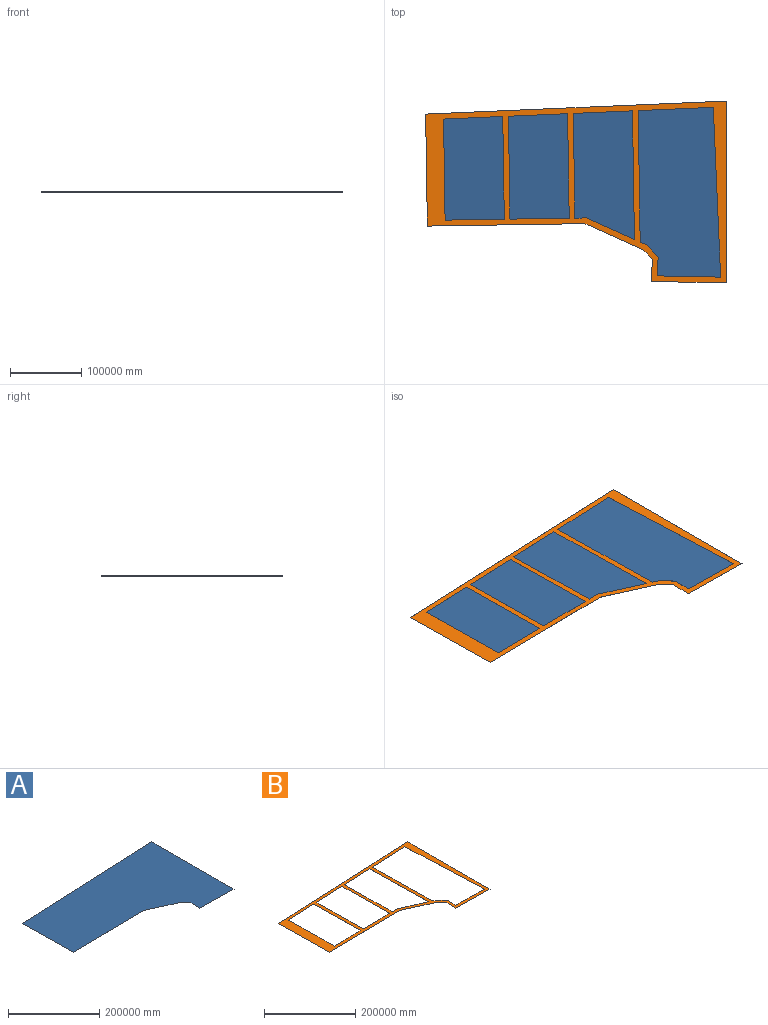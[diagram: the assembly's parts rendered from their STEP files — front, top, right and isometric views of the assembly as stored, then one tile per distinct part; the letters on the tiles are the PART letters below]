
ASSEMBLY  parts=2 mates=1
PART A: 10 faces, bbox 421603.4x255000x25 mm
  f0: plane 421603.41x18291.14mm, normal (-0.04,1,0), area 10550000mm2, adj f1,f7,f8,f9
  f1: plane 156981.63x2401.73mm, normal (-1,-0.02,0), area 3925000mm2, adj f0,f2,f8,f9
  f2: plane 220974.14x3380.78mm, normal (0.02,-1,0), area 5525000mm2, adj f1,f3,f8,f9
  f3: plane 81227.35x36374.69mm, normal (-0.41,-0.91,0), area 2225000mm2, adj f2,f4,f8,f9
  f4: plane 13695.87x13169.02mm, normal (-0.72,-0.69,0), area 475000mm2, adj f3,f5,f8,f9
  f5: plane 30978.71x1148.65mm, normal (-1,0.04,0), area 775000mm2, adj f4,f6,f8,f9
  f6: plane 104979.82x2058.74mm, normal (-0.02,-1,0), area 2625000mm2, adj f5,f7,f8,f9
  f7: plane 255000x25mm, normal (1,0,0), area 6375000mm2, adj f0,f6,f8,f9
  f8: plane 421603.41x255000mm, normal (0,0,1), area 79395387368.9mm2, adj f0,f1,f2,f3,f4,f5,f6,f7
  f9: plane 421603.41x255000mm, normal (0,0,-1), area 79395387368.9mm2, adj f0,f1,f2,f3,f4,f5,f6,f7
PART B: 30 faces, bbox 421603.4x255000x25 mm
  f0: plane 421603.41x18291.14mm, normal (-0.04,1,0), area 10550000mm2, adj f1,f27,f28,f29
  f1: plane 156981.63x2401.73mm, normal (-1,-0.02,0), area 3925000mm2, adj f0,f2,f28,f29
  f2: plane 220974.14x3380.78mm, normal (0.02,-1,0), area 5525000mm2, adj f1,f3,f28,f29
  f3: plane 81227.35x36374.69mm, normal (-0.41,-0.91,0), area 2225000mm2, adj f2,f4,f28,f29
  f4: plane 13695.87x13169.02mm, normal (-0.72,-0.69,0), area 475000mm2, adj f3,f5,f28,f29
  f5: plane 30978.71x1148.65mm, normal (-1,0.04,0), area 775000mm2, adj f4,f6,f28,f29
  f6: plane 104979.82x2058.74mm, normal (-0.02,-1,0), area 2625000mm2, adj f5,f27,f28,f29
  f7: plane 141681.93x2167.66mm, normal (1,0.02,0), area 3542462.9mm2, adj f8,f23,f28,f29
  f8: plane 82954.65x3598.96mm, normal (0.04,-1,0), area 2075817.1mm2, adj f7,f9,f28,f29
  f9: plane 144011.19x2203.29mm, normal (-1,-0.02,0), area 3600701.1mm2, adj f8,f23,f28,f29
  f10: plane 144235.7x2206.73mm, normal (1,0.02,0), area 3606314.4mm2, adj f11,f24,f28,f29
  f11: plane 82954.65x3598.96mm, normal (0.04,-1,0), area 2075817.1mm2, adj f10,f12,f28,f29
  f12: plane 146564.96x2242.36mm, normal (-1,-0.02,0), area 3664552.7mm2, adj f11,f24,f28,f29
  f13: plane 15771.71x241.3mm, normal (-0.02,1,0), area 394338.9mm2, adj f14,f25,f28,f29
  f14: plane 146789.46x2245.8mm, normal (1,0.02,0), area 3670166mm2, adj f13,f15,f28,f29
  f15: plane 82954.65x3598.96mm, normal (0.04,-1,0), area 2075817.1mm2, adj f14,f16,f28,f29
  f16: plane 180463.26x2760.99mm, normal (-1,-0.02,0), area 4512109.4mm2, adj f15,f25,f28,f29
  f17: plane 8510.99x3811.33mm, normal (0.41,0.91,0), area 233135.1mm2, adj f18,f26,f28,f29
  f18: plane 184417.79x2821.49mm, normal (1,0.02,0), area 4610984.2mm2, adj f17,f19,f28,f29
  f19: plane 105316.55x4569.13mm, normal (0.04,-1,0), area 2635390.5mm2, adj f18,f20,f28,f29
  f20: plane 238038.93x10327.25mm, normal (-1,-0.04,0), area 5956571.1mm2, adj f19,f21,f28,f29
  f21: plane 88683.66x1739.16mm, normal (0.02,1,0), area 2217517.9mm2, adj f20,f22,f28,f29
  f22: plane 26236.91x972.83mm, normal (1,-0.04,0), area 656373.5mm2, adj f21,f26,f28,f29
  f23: plane 82990.29x1269.71mm, normal (-0.02,1,0), area 2075000mm2, adj f7,f9,f28,f29
  f24: plane 82990.29x1269.71mm, normal (-0.02,1,0), area 2075000mm2, adj f10,f12,f28,f29
  f25: plane 67698.13x30316.13mm, normal (0.41,0.91,0), area 1854404.3mm2, adj f13,f16,f28,f29
  f26: plane 17264.61x16600.49mm, normal (0.72,0.69,0), area 598771mm2, adj f17,f22,f28,f29
  f27: plane 255000x25mm, normal (1,0,0), area 6375000mm2, adj f0,f6,f28,f29
  f28: plane 421603.41x255000mm, normal (0,0,1), area 17544983656.3mm2, adj f0,f1,f2,f3,f4,f5,f6,f7
  f29: plane 421603.41x255000mm, normal (0,0,-1), area 17544983656.3mm2, adj f0,f1,f2,f3,f4,f5,f6,f7
PLACE A t=(-31294.56,-14442.72,-79.89)mm fixed
PLACE B t=(-34125.42,-13551.6,-54.89)mm
MATE fastened A.f8 <-> B.f29  axis (0,0,1) through (-207437.79,90628.56,-54.89)mm
